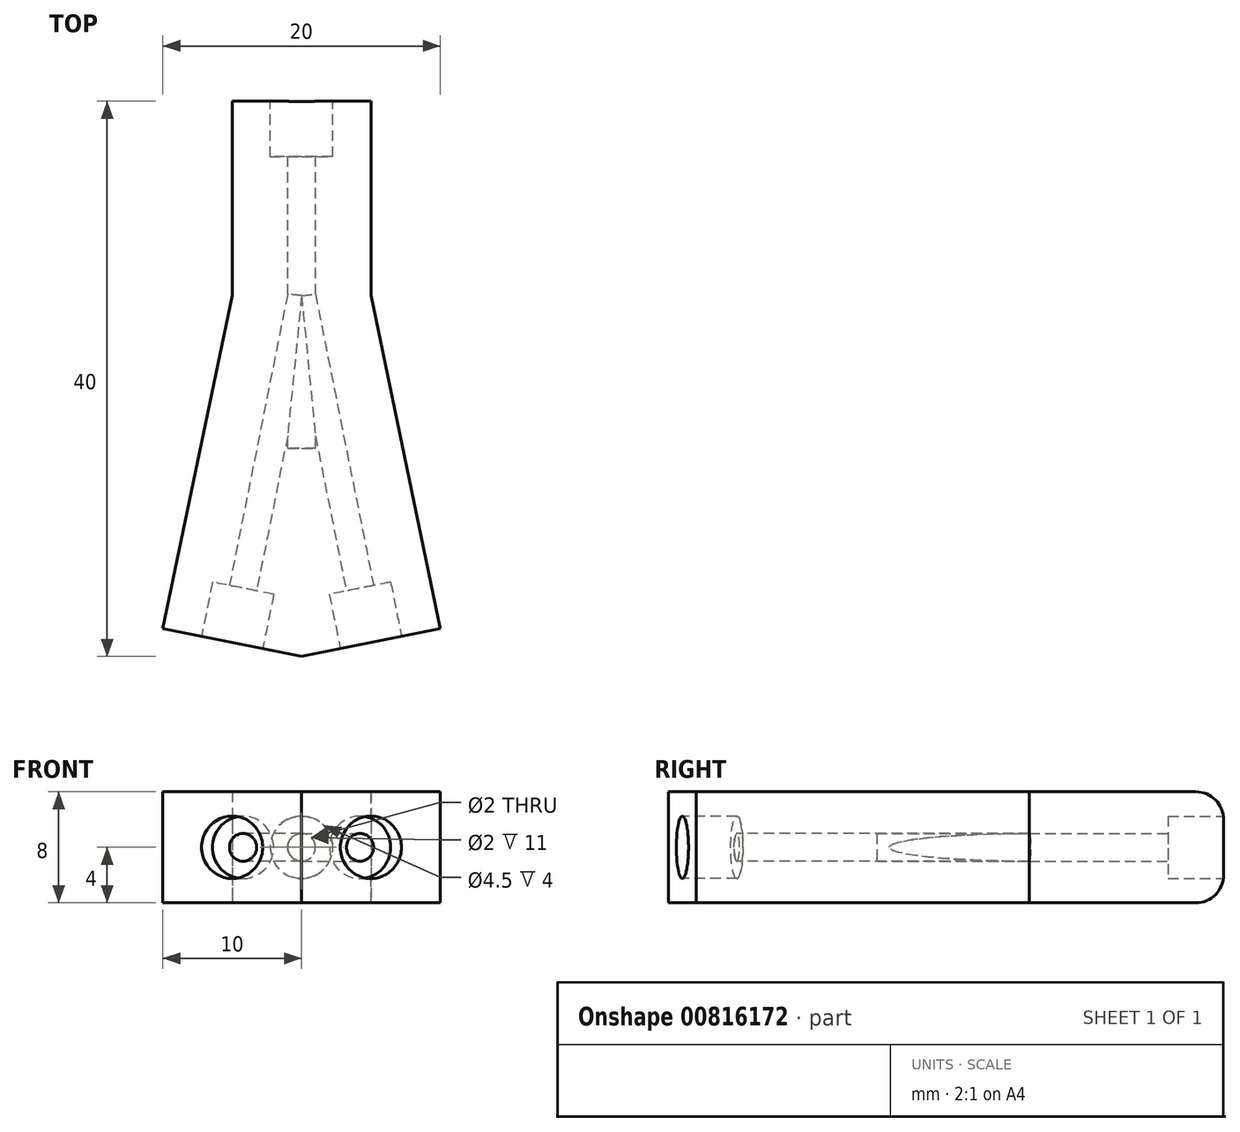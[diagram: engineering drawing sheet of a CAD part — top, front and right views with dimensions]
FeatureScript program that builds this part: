
annotation { "Feature Type Name" : "Feature", "Feature Type Description" : "" }
export const myFeature = defineFeature(function(context is Context, id is Id, definition is map)
    precondition{}
    {
        {
            var Q0;
            Q0=qCreatedBy(makeId("Top.planeOp"),FACE);
            var sketch = newSketch(context, id + "F0", { "sketchPlane" : qUnion([Q0])});
            skLineSegment(sketch, "E0.bottom", {"start": v(-10, -20) * mm, "end": v(10, -20) * mm});
            skLineSegment(sketch, "E0.top", {"start": v(-10, 20) * mm, "end": v(10, 20) * mm});
            skLineSegment(sketch, "E0.left", {"start": v(-10, -20) * mm, "end": v(-10, 20) * mm});
            skLineSegment(sketch, "E0.right", {"start": v(10, -20) * mm, "end": v(10, 20) * mm});
            skPoint(sketch, "E0.middle", {"position": v(0, 0) * mm});
            skSolve(sketch);
        }
        {
            var Q0;
            Q0=makeQuery(id+"F0.imprint","IMPRINT",FACE,{"disambiguationData":[TD([[makeQuery(id+"F0.imprint","IMPRINT",EDGE,{"derivedFrom":sQuery(id+"F0.wireOp",EDGE,"E0.bottom")}),1.0]])]});
            extrude(context, id + "F1", {"entities" : qUnion([Q0]), "depth" : 8 * mm, "offsetDistance" : 25 * mm});
        }
        {
            var Q0;
            Q0=makeQuery(id+"F1.opExtrude","CAP_FACE",FACE,{"disambiguationData":[OSD([sQuery(id+"F0.wireOp",EDGE,"E0.bottom"),sQuery(id+"F0.wireOp",EDGE,"E0.top"),sQuery(id+"F0.wireOp",EDGE,"E0.left"),sQuery(id+"F0.wireOp",EDGE,"E0.right")])],"isStart":false});
            var sketch = newSketch(context, id + "F2", { "sketchPlane" : qUnion([Q0])});
            skLineSegment(sketch, "E1.bottom", {"start": v(-10, -20) * mm, "end": v(10, -20) * mm});
            skLineSegment(sketch, "E1.top", {"start": v(-10, -18) * mm, "end": v(10, -18) * mm});
            skLineSegment(sketch, "E1.left", {"start": v(-10, -20) * mm, "end": v(-10, -18) * mm});
            skLineSegment(sketch, "E1.right", {"start": v(10, -20) * mm, "end": v(10, -18) * mm});
            skLineSegment(sketch, "E2", {"start": v(-10, -18) * mm, "end": v(0, -20) * mm});
            skLineSegment(sketch, "E3", {"start": v(0, -20) * mm, "end": v(10, -18) * mm});
            skSolve(sketch);
        }
        {
            var Q0;
            {var subQ0=sQuery(id+"F2.wireOp",EDGE,"E1.left");Q0=makeQuery(id+"F2.imprint","IMPRINT",FACE,{"disambiguationData":[TD([[makeQuery(id+"F2.imprint","IMPRINT",EDGE,{"derivedFrom":subQ0}),-1.0]])]});}
            var Q1;
            {var subQ0=sQuery(id+"F2.wireOp",EDGE,"E1.right");Q1=makeQuery(id+"F2.imprint","IMPRINT",FACE,{"disambiguationData":[TD([[makeQuery(id+"F2.imprint","IMPRINT",EDGE,{"derivedFrom":subQ0}),1.0]])]});}
            extrude(context, id + "F3", {"entities" : qUnion([Q0, Q1]), "operationType" : NewBodyOperationType.REMOVE, "endBound" : BoundingType.UP_TO_NEXT, "oppositeDirection" : true, "depth" : 25 * mm, "offsetDistance" : 25 * mm});
        }
        {
            var Q0;
            Q0=makeQuery(id+"F3.boolean.opBoolean","COPY",FACE,{"derivedFrom":makeQuery(id+"F3.opExtrude","SWEPT_FACE",FACE,{"disambiguationData":[OSD([sQuery(id+"F2.wireOp",EDGE,"E3")])]})});
            var sketch = newSketch(context, id + "F4", { "sketchPlane" : qUnion([Q0])});
            skCircle(sketch, "E4", {"center": v(1.18, 4) * mm, "radius": 1 * mm});
            skPoint(sketch, "E4.centerSnap0", {"position": v(-3.92, 4) * mm});
            skPoint(sketch, "E4.centerSnap1", {"position": v(1.18, 8) * mm});
            skSolve(sketch);
        }
        {
            var Q0;
            Q0=makeQuery(id+"F3.boolean.opBoolean","COPY",FACE,{"derivedFrom":makeQuery(id+"F3.opExtrude","SWEPT_FACE",FACE,{"disambiguationData":[OSD([sQuery(id+"F2.wireOp",EDGE,"E2")])]})});
            var sketch = newSketch(context, id + "F5", { "sketchPlane" : qUnion([Q0])});
            skCircle(sketch, "E5", {"center": v(-1.18, 4) * mm, "radius": 1 * mm});
            skPoint(sketch, "E5.centerSnap0", {"position": v(-1.18, 8) * mm});
            skPoint(sketch, "E5.centerSnap1", {"position": v(-6.28, 4) * mm});
            skSolve(sketch);
        }
        {
            var Q0;
            Q0=makeQuery(id+"F1.opExtrude","SWEPT_FACE",FACE,{"disambiguationData":[OSD([sQuery(id+"F0.wireOp",EDGE,"E0.top")])]});
            var sketch = newSketch(context, id + "F6", { "sketchPlane" : qUnion([Q0])});
            skCircle(sketch, "E6", {"center": v(0, 4) * mm, "radius": 1 * mm});
            skPoint(sketch, "E6.centerSnap0", {"position": v(-10, 4) * mm});
            skSolve(sketch);
        }
        {
            var Q0;
            Q0=makeQuery(id+"F6.imprint","IMPRINT",FACE,{"disambiguationData":[TD([[makeQuery(id+"F6.imprint","IMPRINT",EDGE,{"derivedFrom":sQuery(id+"F6.wireOp",EDGE,"E6")}),1.0]])]});
            extrude(context, id + "F7", {"entities" : qUnion([Q0]), "operationType" : NewBodyOperationType.REMOVE, "oppositeDirection" : true, "depth" : 25 * mm, "offsetDistance" : 25 * mm});
        }
        {
            var Q0;
            Q0=makeQuery(id+"F5.imprint","IMPRINT",FACE,{"disambiguationData":[TD([[makeQuery(id+"F5.imprint","IMPRINT",EDGE,{"derivedFrom":sQuery(id+"F5.wireOp",EDGE,"E5")}),1.0]])]});
            extrude(context, id + "F8", {"entities" : qUnion([Q0]), "operationType" : NewBodyOperationType.REMOVE, "endBound" : BoundingType.UP_TO_NEXT, "oppositeDirection" : true, "depth" : 25 * mm, "offsetDistance" : 25 * mm});
        }
        {
            var Q0;
            Q0=makeQuery(id+"F4.imprint","IMPRINT",FACE,{"disambiguationData":[TD([[makeQuery(id+"F4.imprint","IMPRINT",EDGE,{"derivedFrom":sQuery(id+"F4.wireOp",EDGE,"E4")}),1.0]])]});
            extrude(context, id + "F9", {"entities" : qUnion([Q0]), "operationType" : NewBodyOperationType.REMOVE, "endBound" : BoundingType.UP_TO_NEXT, "oppositeDirection" : true, "depth" : 25 * mm, "offsetDistance" : 25 * mm});
        }
        {
            var Q0;
            Q0=makeQuery(id+"F3.boolean.opBoolean","COPY",FACE,{"derivedFrom":makeQuery(id+"F3.opExtrude","SWEPT_FACE",FACE,{"disambiguationData":[OSD([sQuery(id+"F2.wireOp",EDGE,"E2")])]})});
            var sketch = newSketch(context, id + "F10", { "sketchPlane" : qUnion([Q0])});
            skCircle(sketch, "E7", {"center": v(-1.18, 4) * mm, "radius": 2.25 * mm});
            skSolve(sketch);
        }
        {
            var Q0;
            Q0=makeQuery(id+"F3.boolean.opBoolean","COPY",FACE,{"derivedFrom":makeQuery(id+"F3.opExtrude","SWEPT_FACE",FACE,{"disambiguationData":[OSD([sQuery(id+"F2.wireOp",EDGE,"E3")])]})});
            var sketch = newSketch(context, id + "F11", { "sketchPlane" : qUnion([Q0])});
            skCircle(sketch, "E8", {"center": v(1.18, 4) * mm, "radius": 2.25 * mm});
            skSolve(sketch);
        }
        {
            var Q0;
            Q0=makeQuery(id+"F10.imprint","IMPRINT",FACE,{"disambiguationData":[TD([[makeQuery(id+"F10.imprint","IMPRINT",EDGE,{"derivedFrom":sQuery(id+"F10.wireOp",EDGE,"E7")}),1.0]])]});
            extrude(context, id + "F12", {"entities" : qUnion([Q0]), "operationType" : NewBodyOperationType.REMOVE, "oppositeDirection" : true, "depth" : 4 * mm, "offsetDistance" : 25 * mm});
        }
        {
            var Q0;
            Q0=makeQuery(id+"F11.imprint","IMPRINT",FACE,{"disambiguationData":[TD([[makeQuery(id+"F11.imprint","IMPRINT",EDGE,{"derivedFrom":sQuery(id+"F11.wireOp",EDGE,"E8")}),1.0]])]});
            extrude(context, id + "F13", {"entities" : qUnion([Q0]), "operationType" : NewBodyOperationType.REMOVE, "oppositeDirection" : true, "depth" : 4 * mm, "offsetDistance" : 25 * mm});
        }
        {
            var Q0;
            Q0=makeQuery(id+"F1.opExtrude","SWEPT_FACE",FACE,{"disambiguationData":[OSD([sQuery(id+"F0.wireOp",EDGE,"E0.top")])]});
            var sketch = newSketch(context, id + "F14", { "sketchPlane" : qUnion([Q0])});
            skCircle(sketch, "E9", {"center": v(0, 4) * mm, "radius": 2.25 * mm});
            skSolve(sketch);
        }
        {
            var Q0;
            Q0=makeQuery(id+"F14.imprint","IMPRINT",FACE,{"disambiguationData":[TD([[makeQuery(id+"F14.imprint","IMPRINT",EDGE,{"derivedFrom":sQuery(id+"F14.wireOp",EDGE,"E9")}),1.0]])]});
            extrude(context, id + "F15", {"entities" : qUnion([Q0]), "operationType" : NewBodyOperationType.REMOVE, "oppositeDirection" : true, "depth" : 4 * mm, "offsetDistance" : 25 * mm});
        }
        {
            var Q0;
            Q0=makeQuery(id+"F1.opExtrude","SWEPT_FACE",FACE,{"disambiguationData":[OSD([sQuery(id+"F0.wireOp",EDGE,"E0.right")])]});
            var sketch = newSketch(context, id + "F16", { "sketchPlane" : qUnion([Q0])});
            skLineSegment(sketch, "E10.bottom", {"start": v(20, 8) * mm, "end": v(6, 8) * mm});
            skLineSegment(sketch, "E10.top", {"start": v(20, 0) * mm, "end": v(6, 0) * mm});
            skLineSegment(sketch, "E10.left", {"start": v(20, 8) * mm, "end": v(20, 0) * mm});
            skLineSegment(sketch, "E10.right", {"start": v(6, 8) * mm, "end": v(6, 0) * mm});
            skSolve(sketch);
        }
        {
            var Q0;
            Q0=makeQuery(id+"F1.opExtrude","SWEPT_FACE",FACE,{"disambiguationData":[OSD([sQuery(id+"F0.wireOp",EDGE,"E0.left")])]});
            var sketch = newSketch(context, id + "F17", { "sketchPlane" : qUnion([Q0])});
            skLineSegment(sketch, "E11.bottom", {"start": v(-20, 8) * mm, "end": v(-6, 8) * mm});
            skLineSegment(sketch, "E11.top", {"start": v(-20, 0) * mm, "end": v(-6, 0) * mm});
            skLineSegment(sketch, "E11.left", {"start": v(-20, 8) * mm, "end": v(-20, 0) * mm});
            skLineSegment(sketch, "E11.right", {"start": v(-6, 8) * mm, "end": v(-6, 0) * mm});
            skSolve(sketch);
        }
        {
            var Q0;
            Q0=makeQuery(id+"F16.imprint","IMPRINT",FACE,{"disambiguationData":[TD([[makeQuery(id+"F16.imprint","IMPRINT",EDGE,{"derivedFrom":sQuery(id+"F16.wireOp",EDGE,"E10.bottom")}),-1.0]])]});
            extrude(context, id + "F18", {"entities" : qUnion([Q0]), "operationType" : NewBodyOperationType.REMOVE, "oppositeDirection" : true, "depth" : 5 * mm, "offsetDistance" : 25 * mm});
        }
        {
            var Q0;
            Q0=makeQuery(id+"F17.imprint","IMPRINT",FACE,{"disambiguationData":[TD([[makeQuery(id+"F17.imprint","IMPRINT",EDGE,{"derivedFrom":sQuery(id+"F17.wireOp",EDGE,"E11.bottom")}),1.0]])]});
            extrude(context, id + "F19", {"entities" : qUnion([Q0]), "operationType" : NewBodyOperationType.REMOVE, "oppositeDirection" : true, "depth" : 5 * mm, "offsetDistance" : 25 * mm});
        }
        {
            var Q0;
            Q0=makeQuery(id+"F1.opExtrude","CAP_FACE",FACE,{"disambiguationData":[OSD([sQuery(id+"F0.wireOp",EDGE,"E0.bottom"),sQuery(id+"F0.wireOp",EDGE,"E0.top"),sQuery(id+"F0.wireOp",EDGE,"E0.left"),sQuery(id+"F0.wireOp",EDGE,"E0.right")])],"isStart":false});
            var sketch = newSketch(context, id + "F20", { "sketchPlane" : qUnion([Q0])});
            skLineSegment(sketch, "E12", {"start": v(5, 6) * mm, "end": v(10, -18) * mm});
            skLineSegment(sketch, "E13", {"start": v(-5, 6) * mm, "end": v(-10, -18) * mm});
            skSolve(sketch);
        }
        {
            var Q0;
            Q0=makeQuery(id+"F20.imprint","IMPRINT",FACE,{"disambiguationData":[TD([[makeQuery(id+"F20.imprint","IMPRINT",EDGE,{"derivedFrom":sQuery(id+"F20.wireOp",EDGE,"E13")}),-1.0]])]});
            var Q1;
            Q1=makeQuery(id+"F20.imprint","IMPRINT",FACE,{"disambiguationData":[TD([[makeQuery(id+"F20.imprint","IMPRINT",EDGE,{"derivedFrom":sQuery(id+"F20.wireOp",EDGE,"E12")}),1.0]])]});
            extrude(context, id + "F21", {"entities" : qUnion([Q0, Q1]), "operationType" : NewBodyOperationType.REMOVE, "endBound" : BoundingType.UP_TO_NEXT, "oppositeDirection" : true, "depth" : 25 * mm, "offsetDistance" : 25 * mm});
        }
        {
            var Q0;
            Q0=makeQuery(id+"F18.boolean.opBoolean","COPY",EDGE,{"derivedFrom":makeQuery(id+"F18.opExtrude","CAP_EDGE",EDGE,{"disambiguationData":[OSD([sQuery(id+"F16.wireOp",EDGE,"E10.bottom")])],"isStart":false})});
            var Q1;
            Q1=makeQuery(id+"F18.boolean.opBoolean","COPY",EDGE,{"derivedFrom":makeQuery(id+"F18.opExtrude","CAP_EDGE",EDGE,{"disambiguationData":[OSD([sQuery(id+"F16.wireOp",EDGE,"E10.top")])],"isStart":false})});
            var Q2;
            Q2=makeQuery(id+"F21.boolean.opBoolean","COPY",EDGE,{"derivedFrom":makeQuery(id+"F21.opExtrude","CAP_EDGE",EDGE,{"disambiguationData":[OSD([sQuery(id+"F20.wireOp",EDGE,"E12")])],"isStart":true})});
            var Q3;
            Q3=makeQuery(id+"F21.boolean.opBoolean","COPY",EDGE,{"derivedFrom":makeQuery(id+"F21.opExtrude","TWEAK_EDGE",EDGE,{"derivedFrom":[makeQuery(id+"F1.opExtrude","CAP_FACE",FACE,{"disambiguationData":[OSD([sQuery(id+"F0.wireOp",EDGE,"E0.bottom"),sQuery(id+"F0.wireOp",EDGE,"E0.top"),sQuery(id+"F0.wireOp",EDGE,"E0.left"),sQuery(id+"F0.wireOp",EDGE,"E0.right")])],"isStart":true}),makeQuery(id+"F20.imprint","IMPRINT",EDGE,{"derivedFrom":sQuery(id+"F20.wireOp",EDGE,"E12")})]})});
            var Q4;
            Q4=makeQuery(id+"F21.boolean.opBoolean","COPY",EDGE,{"derivedFrom":makeQuery(id+"F21.opExtrude","CAP_EDGE",EDGE,{"disambiguationData":[OSD([sQuery(id+"F20.wireOp",EDGE,"E13")])],"isStart":true})});
            var Q5;
            Q5=makeQuery(id+"F19.boolean.opBoolean","COPY",EDGE,{"derivedFrom":makeQuery(id+"F19.opExtrude","CAP_EDGE",EDGE,{"disambiguationData":[OSD([sQuery(id+"F17.wireOp",EDGE,"E11.bottom")])],"isStart":false})});
            var Q6;
            Q6=makeQuery(id+"F21.boolean.opBoolean","COPY",EDGE,{"derivedFrom":makeQuery(id+"F21.opExtrude","TWEAK_EDGE",EDGE,{"derivedFrom":[makeQuery(id+"F1.opExtrude","CAP_FACE",FACE,{"disambiguationData":[OSD([sQuery(id+"F0.wireOp",EDGE,"E0.bottom"),sQuery(id+"F0.wireOp",EDGE,"E0.top"),sQuery(id+"F0.wireOp",EDGE,"E0.left"),sQuery(id+"F0.wireOp",EDGE,"E0.right")])],"isStart":true}),makeQuery(id+"F20.imprint","IMPRINT",EDGE,{"derivedFrom":sQuery(id+"F20.wireOp",EDGE,"E13")})]})});
            var Q7;
            Q7=makeQuery(id+"F19.boolean.opBoolean","COPY",EDGE,{"derivedFrom":makeQuery(id+"F19.opExtrude","CAP_EDGE",EDGE,{"disambiguationData":[OSD([sQuery(id+"F17.wireOp",EDGE,"E11.top")])],"isStart":false})});
            var Q8;
            Q8=makeQuery(id+"F1.opExtrude","CAP_EDGE",EDGE,{"disambiguationData":[OSD([sQuery(id+"F0.wireOp",EDGE,"E0.top")])],"isStart":true});
            var Q9;
            Q9=makeQuery(id+"F19.boolean.opBoolean","COPY",EDGE,{"derivedFrom":makeQuery(id+"F19.opExtrude","CAP_EDGE",EDGE,{"disambiguationData":[OSD([sQuery(id+"F17.wireOp",EDGE,"E11.left")])],"isStart":false})});
            var Q10;
            Q10=makeQuery(id+"F1.opExtrude","CAP_EDGE",EDGE,{"disambiguationData":[OSD([sQuery(id+"F0.wireOp",EDGE,"E0.top")])],"isStart":false});
            var Q11;
            Q11=makeQuery(id+"F18.boolean.opBoolean","COPY",EDGE,{"derivedFrom":makeQuery(id+"F18.opExtrude","CAP_EDGE",EDGE,{"disambiguationData":[OSD([sQuery(id+"F16.wireOp",EDGE,"E10.left")])],"isStart":false})});
            var Q12;
            {var subQ0=sQuery(id+"F2.wireOp",EDGE,"E3");var subQ1=sQuery(id+"F2.wireOp",EDGE,"E1.right");var subQ2=sQuery(id+"F2.wireOp",EDGE,"E1.top");var subQ3=sQuery(id+"F0.wireOp",EDGE,"E0.right");Q12=makeQuery(id+"F21.boolean.opBoolean","MERGE",EDGE,{"derivedFrom":[makeQuery(id+"F3.boolean.opBoolean","COPY",EDGE,{"derivedFrom":makeQuery(id+"F3.opExtrude","SWEPT_EDGE",EDGE,{"disambiguationData":[OSD([subQ3,subQ2,subQ1,subQ0])]})}),makeQuery(id+"F21.opExtrude","SWEPT_EDGE",EDGE,{"disambiguationData":[OSD([subQ3,subQ2,subQ1,subQ0,sQuery(id+"F20.wireOp",EDGE,"E12")])]})]});}
            var Q13;
            {var subQ0=sQuery(id+"F2.wireOp",EDGE,"E2");var subQ1=sQuery(id+"F2.wireOp",EDGE,"E1.left");var subQ2=sQuery(id+"F2.wireOp",EDGE,"E1.top");var subQ3=sQuery(id+"F0.wireOp",EDGE,"E0.left");Q13=makeQuery(id+"F21.boolean.opBoolean","MERGE",EDGE,{"derivedFrom":[makeQuery(id+"F3.boolean.opBoolean","COPY",EDGE,{"derivedFrom":makeQuery(id+"F3.opExtrude","SWEPT_EDGE",EDGE,{"disambiguationData":[OSD([subQ3,subQ2,subQ1,subQ0])]})}),makeQuery(id+"F21.opExtrude","SWEPT_EDGE",EDGE,{"disambiguationData":[OSD([sQuery(id+"F0.wireOp",EDGE,"E0.bottom"),sQuery(id+"F0.wireOp",EDGE,"E0.top"),subQ3,sQuery(id+"F0.wireOp",EDGE,"E0.right"),subQ2,subQ1,subQ0])]})]});}
            var Q14;
            {var subQ0=sQuery(id+"F2.wireOp",EDGE,"E3");var subQ1=sQuery(id+"F2.wireOp",EDGE,"E2");var subQ2=sQuery(id+"F2.wireOp",EDGE,"E1.bottom");Q14=makeQuery(id+"F3.boolean.opBoolean","TWEAK_EDGE",EDGE,{"derivedFrom":[makeQuery(id+"F3.opExtrude","SWEPT_EDGE",EDGE,{"disambiguationData":[OSD([subQ2,subQ1,subQ0]),OD(0.0)]}),makeQuery(id+"F3.opExtrude","SWEPT_EDGE",EDGE,{"disambiguationData":[OSD([subQ2,subQ1,subQ0]),OD(1.0)]})]});}
            var Q15;
            Q15=makeQuery(id+"F3.boolean.opBoolean","COPY",EDGE,{"derivedFrom":makeQuery(id+"F3.opExtrude","CAP_EDGE",EDGE,{"disambiguationData":[OSD([sQuery(id+"F2.wireOp",EDGE,"E3")])],"isStart":true})});
            var Q16;
            Q16=makeQuery(id+"F3.boolean.opBoolean","COPY",EDGE,{"derivedFrom":makeQuery(id+"F3.opExtrude","CAP_EDGE",EDGE,{"disambiguationData":[OSD([sQuery(id+"F2.wireOp",EDGE,"E2")])],"isStart":true})});
            var Q17;
            Q17=makeQuery(id+"F3.boolean.opBoolean","COPY",EDGE,{"derivedFrom":makeQuery(id+"F3.opExtrude","TWEAK_EDGE",EDGE,{"derivedFrom":[makeQuery(id+"F1.opExtrude","CAP_FACE",FACE,{"disambiguationData":[OSD([sQuery(id+"F0.wireOp",EDGE,"E0.bottom"),sQuery(id+"F0.wireOp",EDGE,"E0.top"),sQuery(id+"F0.wireOp",EDGE,"E0.left"),sQuery(id+"F0.wireOp",EDGE,"E0.right")])],"isStart":true}),makeQuery(id+"F2.imprint","IMPRINT",EDGE,{"derivedFrom":sQuery(id+"F2.wireOp",EDGE,"E2")})]})});
            var Q18;
            Q18=makeQuery(id+"F3.boolean.opBoolean","COPY",EDGE,{"derivedFrom":makeQuery(id+"F3.opExtrude","TWEAK_EDGE",EDGE,{"derivedFrom":[makeQuery(id+"F1.opExtrude","CAP_FACE",FACE,{"disambiguationData":[OSD([sQuery(id+"F0.wireOp",EDGE,"E0.bottom"),sQuery(id+"F0.wireOp",EDGE,"E0.top"),sQuery(id+"F0.wireOp",EDGE,"E0.left"),sQuery(id+"F0.wireOp",EDGE,"E0.right")])],"isStart":true}),makeQuery(id+"F2.imprint","IMPRINT",EDGE,{"derivedFrom":sQuery(id+"F2.wireOp",EDGE,"E3")})]})});
            fillet(context, id + "F22", {"entities" : qUnion([Q0, Q1, Q2, Q3, Q4, Q5, Q6, Q7, Q8, Q9, Q10, Q11, Q12, Q13, Q14, Q15, Q16, Q17, Q18]), "radius" : 2 * mm, "tangentPropagation" : true, "allowEdgeOverflow" : false});
        }
    });
